# Revit family: 00-8317-60-60
name_source: partatom
category: Luminarias
units: mm (PartAtom-declared; Revit-internal decimal feet)

## family parameters
Anfitrión = Cara
Compartido = Sí
Corte con vacíos al cargar = No
Cota de conector redondo = Diámetro de uso
Número OmniClass = 23.80.70.00
Origen de luz = No
Punto de cálculo de habitación = No
Tipo de pieza = Normal
Título OmniClass = Lighting

## types (1)
- 00-8317-60-60
    Acabado = Black, Transparent
    CRI = 90
    Carga aparente = 0 VA
    Catálogo = Decorative
    CodigoGubimclass = 50.60.50.20
    CodigoOmniclass = 21-04 50 40
    CodigoUniclass2015 = EF_70_80
    CodigoUniformat2010 = D5040
    DescripcionGubimclass = Iluminación interior
    DescripcionOmniclass = Lighting
    DescripcionUniclass2015 = Lighting
    DescripcionUniformat2010 = Lighting
    EAN13 = 8435575369344
    Eficiencia energética = F
    Elevación por defecto = 1000 mm  [stored 3.28084 ft]
    Etiqueta V/f = 100-240V/50-60Hz
    Fabricante = LEDS C4
    Familia = Candle 5 Bodies Chandelier
    FechaVersion = Creada: 23/12/2022
    Ficha = https://files.leds-c4.com
    Fotometría = https://files.leds-c4.com
    IMC = https://files.leds-c4.com
    IP = IP20
    IfcExportAs = IfcLightFixture
IfcLightFixture
    IfcExportType = NOTDEFINED
    Imagen web = https://files.leds-c4.com
    LDT = https://files.leds-c4.com
    Lumenes reales (lm) = 844
    Material = Steel, Aluminium, Methacrylate
    Peso neto (KG) = 2.6
    Producto descatalogado = Catalogado EN
    Referencia = 00-8317-60-60
    Temperatura color led (K) = LED warm-white 2700K
    Tender text (Castellano) = LEDS C4 Candle 5 Bodies Chandelier 00-8317-60-60  Pendant for indoor use.   For downlighting. Structure material: Steel, Aluminium. Structure finish: Black. Diffuser material: Methacrylate. Diffuser finish: Transparent. Warranty: 5 Years.  Product net weight (Kg): 2.6 Product width or diameter (mm): 220 Product height (mm): 350-3000  Class 1. IP: IP20. LED. No. of lampholders or LEDs: 1. LED brand: CREE. Driver brand: TCI. Maximum power of light source: 15.6W. Colour temperature: 2700K. Colour rendering index: 90. MacAdam Steps: 2. Hours of life: 50.000h L80B20. UGR: 22.4. Photobiological risk: RG1. % de Flickering: &lt;5%. Real flux (lm): 844. Real lm/W: 50. Voltage / frequency range: 99-264/50-60Hz. Voltage: 9. Equipment included: Yes. Total power: 16.8. Power factor: 0.96. Dimmable equipment included: 0-10V / 1-10V / PUSH/ DALI.
    Tender text (English) = LEDS C4 Candle 5 Bodies Chandelier 00-8317-60-60  Pendant for indoor use.   For downlighting. Structure material: Steel, Aluminium. Structure finish: Black. Diffuser material: Methacrylate. Diffuser finish: Transparent. Warranty: 5 Years.  Product net weight (Kg): 2.6 Product width or diameter (mm): 220 Product height (mm): 350-3000  Class 1. IP: IP20. LED. No. of lampholders or LEDs: 1. LED brand: CREE. Driver brand: TCI. Maximum power of light source: 15.6W. Colour temperature: 2700K. Colour rendering index: 90. MacAdam Steps: 2. Hours of life: 50.000h L80B20. UGR: 22.4. Photobiological risk: RG1. % de Flickering: &lt;5%. Real flux (lm): 844. Real lm/W: 50. Voltage / frequency range: 99-264/50-60Hz. Voltage: 9. Equipment included: Yes. Total power: 16.8. Power factor: 0.96. Dimmable equipment included: 0-10V / 1-10V / PUSH/ DALI.
    Tipo = Pendant
    Tipo de regulación = 0-10V / 1-10V / PUSH/ DALI
    Vatios (W) = 16.8
    Versión = v1

note: [stored X ft] marks values corroborated as IEEE doubles in the binary element streams (Revit-internal decimal feet)
